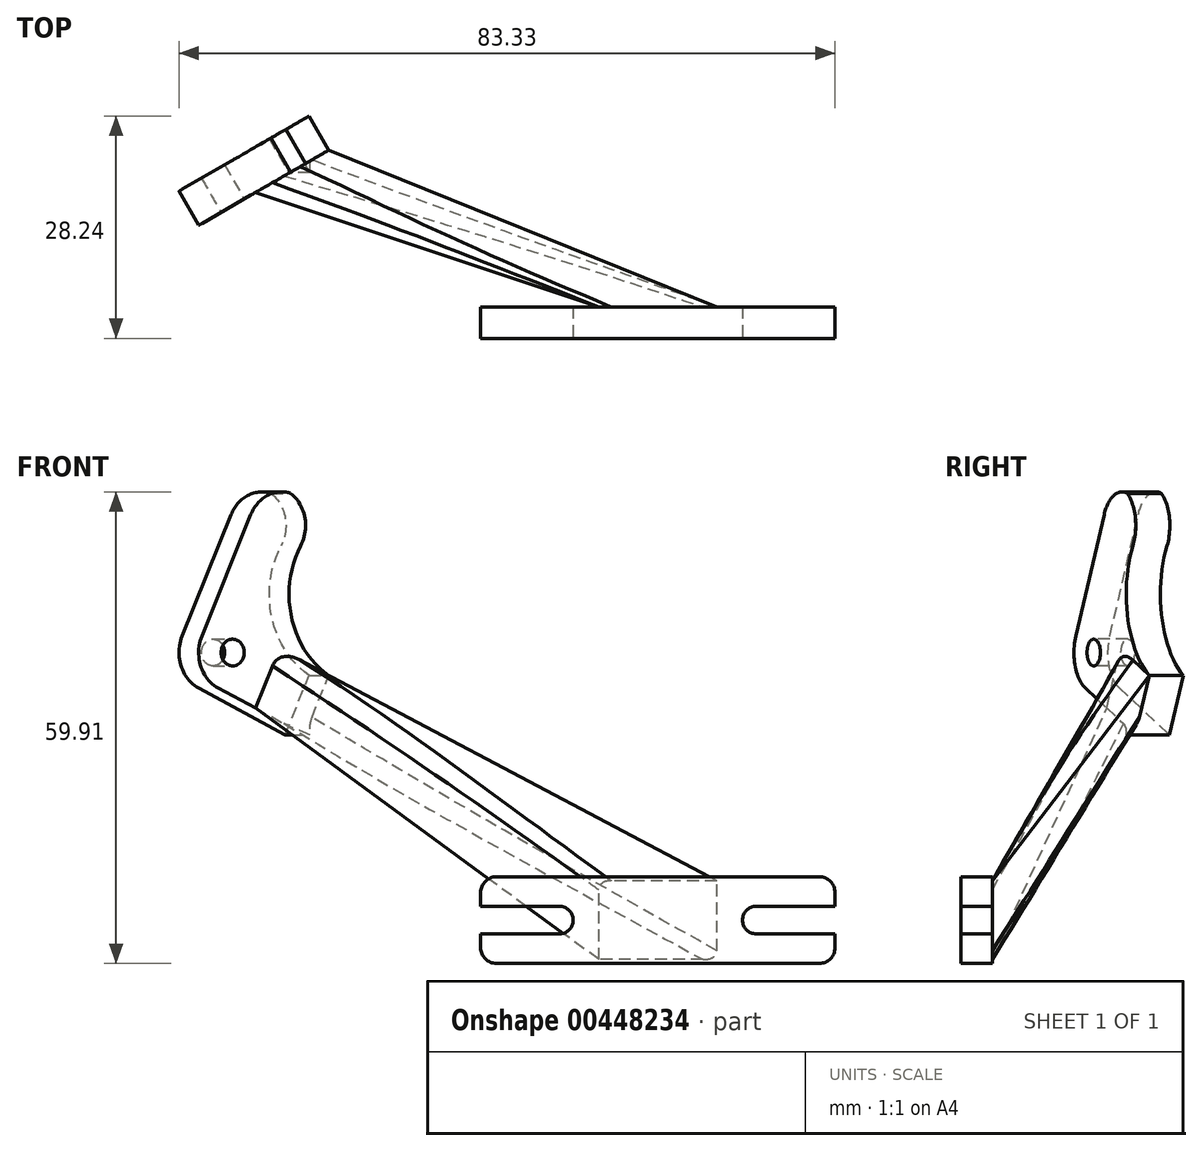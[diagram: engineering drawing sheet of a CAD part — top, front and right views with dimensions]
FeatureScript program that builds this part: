
annotation { "Feature Type Name" : "Feature", "Feature Type Description" : "" }
export const myFeature = defineFeature(function(context is Context, id is Id, definition is map)
    precondition{}
    {
        {
            var Q0;
            Q0=qCreatedBy(makeId("Top.planeOp"),FACE);
            var sketch = newSketch(context, id + "F0", { "sketchPlane" : qUnion([Q0])});
            skLineSegment(sketch, "E0", {"start": v(0, 0) * mm, "end": v(36.98, 21.35) * mm});
            skLineSegment(sketch, "E1", {"start": v(36.98, 21.35) * mm, "end": v(-36.5, -21.07) * mm});
            skSolve(sketch);
        }
        {
            var Q0;
            Q0=qCreatedBy(makeId("Front.planeOp"),FACE);
            var sketch = newSketch(context, id + "F1", { "sketchPlane" : qUnion([Q0])});
            skPoint(sketch, "E2", {"position": v(0, 53.35) * mm});
            skSolve(sketch);
        }
        {
            var Q0;
            Q0=sQuery(id+"F0.wireOp",VERTEX,"E1.end");
            var Q1;
            Q1=sQuery(id+"F0.wireOp",VERTEX,"E0.end");
            var Q2;
            Q2=sQuery(id+"F1.wireOp",VERTEX,"E2");
            cPlane(context, id + "F2", {"entities" : qUnion([Q0, Q1, Q2]), "cplaneType" : CPlaneType.THREE_POINT, "offset" : 25 * mm, "width" : 150 * mm, "height" : 150 * mm});
        }
        {
            var Q0;
            Q0=qCreatedBy(id+"F2.planeOp",FACE);
            var sketch = newSketch(context, id + "F3", { "sketchPlane" : qUnion([Q0])});
            skLineSegment(sketch, "E3.bottom", {"start": v(7.38, 20.27) * mm, "end": v(-20.27, 7.38) * mm, "construction": true});
            skLineSegment(sketch, "E3.top", {"start": v(20.27, -7.38) * mm, "end": v(-7.38, -20.27) * mm, "construction": true});
            skLineSegment(sketch, "E3.left", {"start": v(7.38, 20.27) * mm, "end": v(20.27, -7.38) * mm, "construction": true});
            skLineSegment(sketch, "E3.right", {"start": v(-20.27, 7.38) * mm, "end": v(-7.38, -20.27) * mm, "construction": true});
            skPoint(sketch, "E3.middle", {"position": v(0, 0) * mm});
            skLineSegment(sketch, "E4", {"start": v(24.8, -5.26) * mm, "end": v(15.5, 14.68) * mm});
            skCircle(sketch, "E5", {"center": v(0, 0) * mm, "radius": 11 * mm, "construction": true});
            skArc(sketch, "E6", {"start": v(24.8, -5.26) * mm, "mid": v(24.96, -9.09) * mm, "end": v(22.38, -11.9) * mm});
            skLineSegment(sketch, "E7", {"start": v(22.38, -11.9) * mm, "end": v(9.7, -17.82) * mm});
            skCircle(sketch, "E8", {"center": v(20.27, -7.38) * mm, "radius": 1.7 * mm});
            skLineSegment(sketch, "E9", {"start": v(15.5, 14.68) * mm, "end": v(6.14, 10.31) * mm});
            skArc(sketch, "E10", {"start": v(6.14, 10.31) * mm, "mid": v(12, 0.02) * mm, "end": v(6.18, -10.29) * mm});
            skLineSegment(sketch, "E11", {"start": v(9.7, -17.82) * mm, "end": v(6.18, -10.29) * mm});
            skSolve(sketch);
        }
        {
            var Q0;
            Q0=qCreatedBy(makeId("Front.planeOp"),FACE);
            cPlane(context, id + "F4", {"entities" : qUnion([Q0]), "cplaneType" : CPlaneType.OFFSET, "offset" : 23 * mm, "width" : 150 * mm, "height" : 150 * mm});
        }
        {
            var Q0;
            Q0=qCreatedBy(id+"F4.planeOp",FACE);
            var sketch = newSketch(context, id + "F5", { "sketchPlane" : qUnion([Q0])});
            skLineSegment(sketch, "E12.bottom", {"start": v(43.95, -46.38) * mm, "end": v(28.95, -46.38) * mm});
            skLineSegment(sketch, "E12.top", {"start": v(43.95, -36.38) * mm, "end": v(28.95, -36.38) * mm});
            skLineSegment(sketch, "E12.left", {"start": v(43.95, -46.38) * mm, "end": v(43.95, -36.38) * mm});
            skLineSegment(sketch, "E12.right", {"start": v(28.95, -46.38) * mm, "end": v(28.95, -36.38) * mm});
            skPoint(sketch, "E12.middle", {"position": v(36.45, -41.38) * mm});
            skSolve(sketch);
        }
        {
            var Q0;
            Q0 = qSketchRegion(id + "F3", true);
            extrude(context, id + "F6", {"entities" : qUnion([Q0]), "depth" : 5 * mm});
        }
        {
            var Q0;
            Q0=makeQuery(id+"F6.opExtrude","CAP_FACE",FACE,{"disambiguationData":[OSD([sQuery(id+"F3.wireOp",EDGE,"E4"),sQuery(id+"F3.wireOp",EDGE,"E6"),sQuery(id+"F3.wireOp",EDGE,"E7"),sQuery(id+"F3.wireOp",EDGE,"E8"),sQuery(id+"F3.wireOp",EDGE,"E9"),sQuery(id+"F3.wireOp",EDGE,"E10"),sQuery(id+"F3.wireOp",EDGE,"E11")])],"isStart":true});
            var sketch = newSketch(context, id + "F7", { "sketchPlane" : qUnion([Q0])});
            skLineSegment(sketch, "E13.bottom", {"start": v(-9.7, -17.82) * mm, "end": v(-16.94, -14.44) * mm});
            skLineSegment(sketch, "E13.top", {"start": v(-6.18, -10.29) * mm, "end": v(-13.43, -6.9) * mm});
            skLineSegment(sketch, "E13.left", {"start": v(-9.7, -17.82) * mm, "end": v(-6.18, -10.29) * mm});
            skLineSegment(sketch, "E13.right", {"start": v(-16.94, -14.44) * mm, "end": v(-13.43, -6.9) * mm});
            skSolve(sketch);
        }
        {
            var Q1;
            Q1 = qSketchRegion(id + "F5", true);
            var Q2;
            Q2 = qSketchRegion(id + "F7", true);
            loft(context, id + "F8", {"operationType" : NewBodyOperationType.ADD, "sheetProfilesArray" : [{ "sheetProfileEntities" : qUnion([Q1]) }, { "sheetProfileEntities" : qUnion([Q2]) }]});
        }
        {
            var Q0;
            Q0=makeQuery(id+"F8.opLoft","CAP_FACE",FACE,{"disambiguationData":[OSD([makeQuery(id+"F5.imprint","IMPRINT",FACE,{"disambiguationData":[TD([[makeQuery(id+"F5.imprint","IMPRINT",EDGE,{"derivedFrom":sQuery(id+"F5.wireOp",EDGE,"E12.bottom")}),-1.0]])]})])],"isStart":true});
            var sketch = newSketch(context, id + "F9", { "sketchPlane" : qUnion([Q0])});
            skLineSegment(sketch, "E14.bottom", {"start": v(13.95, -35.88) * mm, "end": v(58.95, -35.88) * mm});
            skLineSegment(sketch, "E14.top", {"start": v(13.95, -46.88) * mm, "end": v(58.95, -46.88) * mm});
            skLineSegment(sketch, "E14.left", {"start": v(13.95, -35.88) * mm, "end": v(13.95, -46.88) * mm});
            skLineSegment(sketch, "E14.right", {"start": v(58.95, -35.88) * mm, "end": v(58.95, -46.88) * mm});
            skLineSegment(sketch, "E15", {"start": v(28.95, -36.38) * mm, "end": v(43.95, -46.38) * mm, "construction": true});
            skLineSegment(sketch, "E16", {"start": v(43.95, -46.38) * mm, "end": v(43.95, -36.38) * mm, "construction": true});
            skLineSegment(sketch, "E17", {"start": v(43.95, -36.38) * mm, "end": v(28.95, -46.38) * mm, "construction": true});
            skLineSegment(sketch, "E18", {"start": v(13.95, -35.88) * mm, "end": v(58.95, -46.88) * mm, "construction": true});
            skLineSegment(sketch, "E19", {"start": v(58.95, -35.88) * mm, "end": v(13.95, -46.88) * mm, "construction": true});
            skPoint(sketch, "E20", {"position": v(36.45, -41.38) * mm});
            skSolve(sketch);
        }
        {
            var Q0;
            Q0=makeQuery(id+"F9.imprint","IMPRINT",FACE,{"disambiguationData":[TD([[makeQuery(id+"F9.imprint","IMPRINT",EDGE,{"derivedFrom":sQuery(id+"F9.wireOp",EDGE,"E14.bottom")}),-1.0]])]});
            var Q1;
            {var subQ0=sQuery(id+"F5.wireOp",EDGE,"E12.right");var subQ1=sQuery(id+"F5.wireOp",EDGE,"E12.left");var subQ2=sQuery(id+"F5.wireOp",EDGE,"E12.bottom");Q1=makeQuery(id+"F9.imprint","IMPRINT",FACE,{"disambiguationData":[TD([[makeQuery(id+"F9.imprint","IMPRINT",EDGE,{"derivedFrom":makeQuery(id+"F8.opLoft","MID_CAP_EDGE",EDGE,{"disambiguationData":[OSD([subQ2,subQ1,subQ0])],"capPos":0.0})}),-1.0]])]});}
            extrude(context, id + "F10", {"entities" : qUnion([Q0, Q1]), "operationType" : NewBodyOperationType.ADD, "depth" : 4 * mm});
        }
        {
            var Q0;
            Q0=makeQuery(id+"F8.opLoft","SWEPT_EDGE",EDGE,{"disambiguationData":[OSD([sQuery(id+"F5.wireOp",EDGE,"E12.top"),sQuery(id+"F5.wireOp",EDGE,"E12.right"),sQuery(id+"F7.wireOp",EDGE,"E13.top"),sQuery(id+"F7.wireOp",EDGE,"E13.right")])]});
            var Q1;
            Q1=makeQuery(id+"F8.opLoft","SWEPT_EDGE",EDGE,{"disambiguationData":[OSD([sQuery(id+"F5.wireOp",EDGE,"E12.bottom"),sQuery(id+"F5.wireOp",EDGE,"E12.left"),sQuery(id+"F7.wireOp",EDGE,"E13.bottom"),sQuery(id+"F7.wireOp",EDGE,"E13.left")])]});
            fillet(context, id + "F11", {"entities" : qUnion([Q0, Q1]), "radius" : 3 * mm, "tangentPropagation" : true, "allowEdgeOverflow" : false});
        }
        {
            var Q0;
            Q0=makeQuery(id+"F10.opExtrude","CAP_FACE",FACE,{"disambiguationData":[OSD([sQuery(id+"F9.wireOp",EDGE,"E14.bottom"),sQuery(id+"F9.wireOp",EDGE,"E14.top"),sQuery(id+"F9.wireOp",EDGE,"E14.left"),sQuery(id+"F9.wireOp",EDGE,"E14.right")])],"isStart":false});
            var sketch = newSketch(context, id + "F12", { "sketchPlane" : qUnion([Q0])});
            skLineSegment(sketch, "E21.bottom", {"start": v(58.95, -39.63) * mm, "end": v(48.95, -39.63) * mm});
            skLineSegment(sketch, "E21.top", {"start": v(58.95, -43.13) * mm, "end": v(48.95, -43.13) * mm});
            skLineSegment(sketch, "E21.left", {"start": v(58.95, -39.63) * mm, "end": v(58.95, -43.13) * mm});
            skLineSegment(sketch, "E21.right", {"start": v(48.95, -39.63) * mm, "end": v(48.95, -43.13) * mm});
            skArc(sketch, "E22", {"start": v(48.95, -39.63) * mm, "mid": v(47.2, -41.38) * mm, "end": v(48.95, -43.13) * mm});
            skLineSegment(sketch, "E23", {"start": v(48.95, -41.38) * mm, "end": v(58.95, -41.38) * mm, "construction": true});
            skLineSegment(sketch, "E24", {"start": v(36.45, -35.88) * mm, "end": v(36.45, -46.88) * mm, "construction": true});
            skLineSegment(sketch, "E25.MirrorCS", {"start": v(13.95, -39.63) * mm, "end": v(13.95, -43.13) * mm});
            skLineSegment(sketch, "E26.MirrorCS", {"start": v(13.95, -39.63) * mm, "end": v(23.95, -39.63) * mm});
            skLineSegment(sketch, "E27.MirrorCS", {"start": v(13.95, -43.13) * mm, "end": v(23.95, -43.13) * mm});
            skArc(sketch, "E28.MirrorCS", {"start": v(23.95, -39.63) * mm, "mid": v(25.7, -41.38) * mm, "end": v(23.95, -43.13) * mm});
            skSolve(sketch);
        }
        {
            var Q0;
            Q0=makeQuery(id+"F12.imprint","IMPRINT",FACE,{"disambiguationData":[TD([[makeQuery(id+"F12.imprint","IMPRINT",EDGE,{"derivedFrom":sQuery(id+"F12.wireOp",EDGE,"E21.bottom")}),1.0]])]});
            var Q1;
            Q1=makeQuery(id+"F12.imprint","IMPRINT",FACE,{"disambiguationData":[TD([[makeQuery(id+"F12.imprint","IMPRINT",EDGE,{"derivedFrom":sQuery(id+"F12.wireOp",EDGE,"E21.right")}),-1.0]])]});
            var Q2;
            Q2=makeQuery(id+"F12.imprint","IMPRINT",FACE,{"disambiguationData":[TD([[makeQuery(id+"F12.imprint","IMPRINT",EDGE,{"derivedFrom":sQuery(id+"F12.wireOp",EDGE,"E25.MirrorCS")}),1.0]])]});
            extrude(context, id + "F13", {"entities" : qUnion([Q0, Q1, Q2]), "operationType" : NewBodyOperationType.REMOVE, "oppositeDirection" : true, "depth" : 5 * mm});
        }
        {
            var Q0;
            Q0=makeQuery(id+"F10.opExtrude","SWEPT_EDGE",EDGE,{"disambiguationData":[OSD([sQuery(id+"F9.wireOp",EDGE,"E14.bottom"),sQuery(id+"F9.wireOp",EDGE,"E14.right")])]});
            var Q1;
            Q1=makeQuery(id+"F10.opExtrude","SWEPT_EDGE",EDGE,{"disambiguationData":[OSD([sQuery(id+"F9.wireOp",EDGE,"E14.bottom"),sQuery(id+"F9.wireOp",EDGE,"E14.left")])]});
            var Q2;
            Q2=makeQuery(id+"F10.opExtrude","SWEPT_EDGE",EDGE,{"disambiguationData":[OSD([sQuery(id+"F9.wireOp",EDGE,"E14.top"),sQuery(id+"F9.wireOp",EDGE,"E14.left")])]});
            var Q3;
            Q3=makeQuery(id+"F10.opExtrude","SWEPT_EDGE",EDGE,{"disambiguationData":[OSD([sQuery(id+"F9.wireOp",EDGE,"E14.top"),sQuery(id+"F9.wireOp",EDGE,"E14.right")])]});
            fillet(context, id + "F14", {"entities" : qUnion([Q0, Q1, Q2, Q3]), "radius" : 2 * mm, "tangentPropagation" : true, "allowEdgeOverflow" : false});
        }
        {
            var Q0;
            Q0=makeQuery(id+"F6.opExtrude","SWEPT_EDGE",EDGE,{"disambiguationData":[OSD([sQuery(id+"F3.wireOp",EDGE,"E4"),sQuery(id+"F3.wireOp",EDGE,"E9")])]});
            var Q1;
            Q1=makeQuery(id+"F6.opExtrude","SWEPT_EDGE",EDGE,{"disambiguationData":[OSD([sQuery(id+"F3.wireOp",EDGE,"E9"),sQuery(id+"F3.wireOp",EDGE,"E10")])]});
            fillet(context, id + "F15", {"entities" : qUnion([Q0, Q1]), "radius" : 5 * mm, "tangentPropagation" : true, "allowEdgeOverflow" : false});
        }
    });
